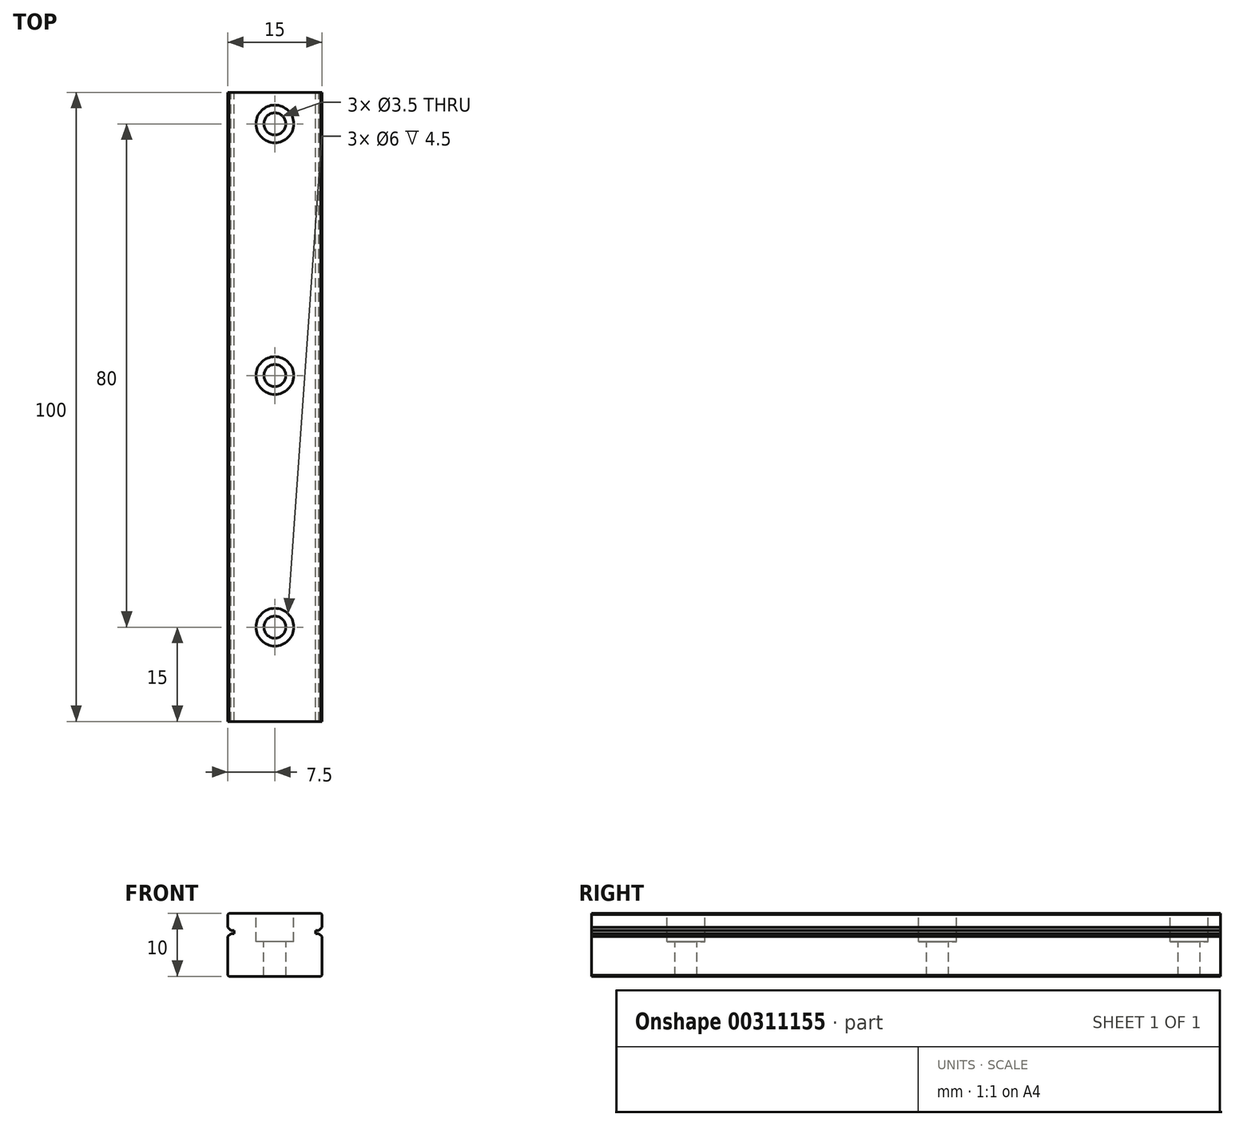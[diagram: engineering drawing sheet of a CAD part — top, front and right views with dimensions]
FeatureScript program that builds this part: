
annotation { "Feature Type Name" : "Feature", "Feature Type Description" : "" }
export const myFeature = defineFeature(function(context is Context, id is Id, definition is map)
    precondition{}
    {
        {
            var Q0;
            Q0=qCreatedBy(makeId("Front.planeOp"),FACE);
            var sketch = newSketch(context, id + "F0", { "sketchPlane" : qUnion([Q0])});
            skLineSegment(sketch, "E0", {"start": v(6.98, 6.35) * mm, "end": v(6.98, 12.45) * mm});
            skLineSegment(sketch, "E1", {"start": v(6.98, 12.45) * mm, "end": v(7.48, 12.95) * mm});
            skLineSegment(sketch, "E2", {"start": v(7.48, 13.45) * mm, "end": v(6.98, 13.95) * mm});
            skLineSegment(sketch, "E3", {"start": v(6.98, 13.95) * mm, "end": v(6.98, 15.95) * mm});
            skLineSegment(sketch, "E4", {"start": v(21.98, 15.95) * mm, "end": v(21.98, 13.95) * mm});
            skLineSegment(sketch, "E5", {"start": v(21.98, 13.95) * mm, "end": v(21.48, 13.45) * mm});
            skLineSegment(sketch, "E6", {"start": v(21.48, 12.95) * mm, "end": v(21.98, 12.45) * mm});
            skLineSegment(sketch, "E7", {"start": v(21.98, 12.45) * mm, "end": v(21.98, 6.35) * mm});
            skLineSegment(sketch, "E8", {"start": v(7.48, 12.95) * mm, "end": v(7.98, 12.95) * mm});
            skLineSegment(sketch, "E9", {"start": v(7.98, 12.95) * mm, "end": v(7.98, 13.45) * mm});
            skLineSegment(sketch, "E10", {"start": v(7.98, 13.45) * mm, "end": v(7.48, 13.45) * mm});
            skLineSegment(sketch, "E11", {"start": v(21.48, 13.45) * mm, "end": v(20.98, 13.45) * mm});
            skLineSegment(sketch, "E12", {"start": v(20.98, 13.45) * mm, "end": v(20.98, 12.95) * mm});
            skLineSegment(sketch, "E13", {"start": v(20.98, 12.95) * mm, "end": v(21.48, 12.95) * mm});
            skLineSegment(sketch, "E14", {"start": v(6.98, 6.35) * mm, "end": v(7.18, 6.15) * mm});
            skLineSegment(sketch, "E15", {"start": v(7.18, 6.15) * mm, "end": v(21.78, 6.15) * mm});
            skLineSegment(sketch, "E16", {"start": v(21.78, 6.15) * mm, "end": v(21.98, 6.35) * mm});
            skLineSegment(sketch, "E17", {"start": v(6.98, 15.95) * mm, "end": v(7.18, 16.15) * mm});
            skLineSegment(sketch, "E18", {"start": v(7.18, 16.15) * mm, "end": v(21.78, 16.15) * mm});
            skLineSegment(sketch, "E19", {"start": v(21.78, 16.15) * mm, "end": v(21.98, 15.95) * mm});
            skSolve(sketch);
        }
        {
            var Q0;
            Q0=makeQuery(id+"F0.imprint","IMPRINT",FACE,{"disambiguationData":[TD([[makeQuery(id+"F0.imprint","IMPRINT",EDGE,{"derivedFrom":sQuery(id+"F0.wireOp",EDGE,"E0")}),-1.0]])]});
            extrude(context, id + "F1", {"entities" : qUnion([Q0]), "depth" : 100 * mm});
        }
        {
            var Q0;
            Q0=makeQuery(id+"F1.opExtrude","SWEPT_FACE",FACE,{"disambiguationData":[OSD([sQuery(id+"F0.wireOp",EDGE,"E18")])]});
            var sketch = newSketch(context, id + "F2", { "sketchPlane" : qUnion([Q0])});
            skCircle(sketch, "E20", {"center": v(14.48, -85) * mm, "radius": 1.75 * mm});
            skPoint(sketch, "E20.centerSnap0", {"position": v(14.48, -100) * mm});
            skCircle(sketch, "E21", {"center": v(14.48, -85) * mm, "radius": 3 * mm});
            skCircle(sketch, "E22.1.0.0", {"center": v(14.48, -45) * mm, "radius": 3 * mm});
            skCircle(sketch, "E22.1.0.1", {"center": v(14.48, -45) * mm, "radius": 1.75 * mm});
            skCircle(sketch, "E22.2.0.0", {"center": v(14.48, -5) * mm, "radius": 3 * mm});
            skCircle(sketch, "E22.2.0.1", {"center": v(14.48, -5) * mm, "radius": 1.75 * mm});
            skLineSegment(sketch, "E22.direction1", {"start": v(14.48, -85) * mm, "end": v(14.48, -45) * mm, "construction": true});
            skSolve(sketch);
        }
        {
            var Q0;
            Q0=makeQuery(id+"F2.imprint","IMPRINT",FACE,{"disambiguationData":[TD([[makeQuery(id+"F2.imprint","IMPRINT",EDGE,{"derivedFrom":sQuery(id+"F2.wireOp",EDGE,"E20")}),1.0]])]});
            var Q1;
            Q1=makeQuery(id+"F2.imprint","IMPRINT",FACE,{"disambiguationData":[TD([[makeQuery(id+"F2.imprint","IMPRINT",EDGE,{"derivedFrom":sQuery(id+"F2.wireOp",EDGE,"E22.1.0.1")}),1.0]])]});
            var Q2;
            Q2=makeQuery(id+"F2.imprint","IMPRINT",FACE,{"disambiguationData":[TD([[makeQuery(id+"F2.imprint","IMPRINT",EDGE,{"derivedFrom":sQuery(id+"F2.wireOp",EDGE,"E22.2.0.1")}),1.0]])]});
            extrude(context, id + "F3", {"entities" : qUnion([Q0, Q1, Q2]), "operationType" : NewBodyOperationType.REMOVE, "endBound" : BoundingType.THROUGH_ALL, "oppositeDirection" : true, "depth" : 25 * mm});
        }
        {
            var Q0;
            Q0 = qSketchRegion(id + "F2", true);
            extrude(context, id + "F4", {"entities" : qUnion([Q0]), "operationType" : NewBodyOperationType.REMOVE, "oppositeDirection" : true, "depth" : 4.5 * mm});
        }
    });
